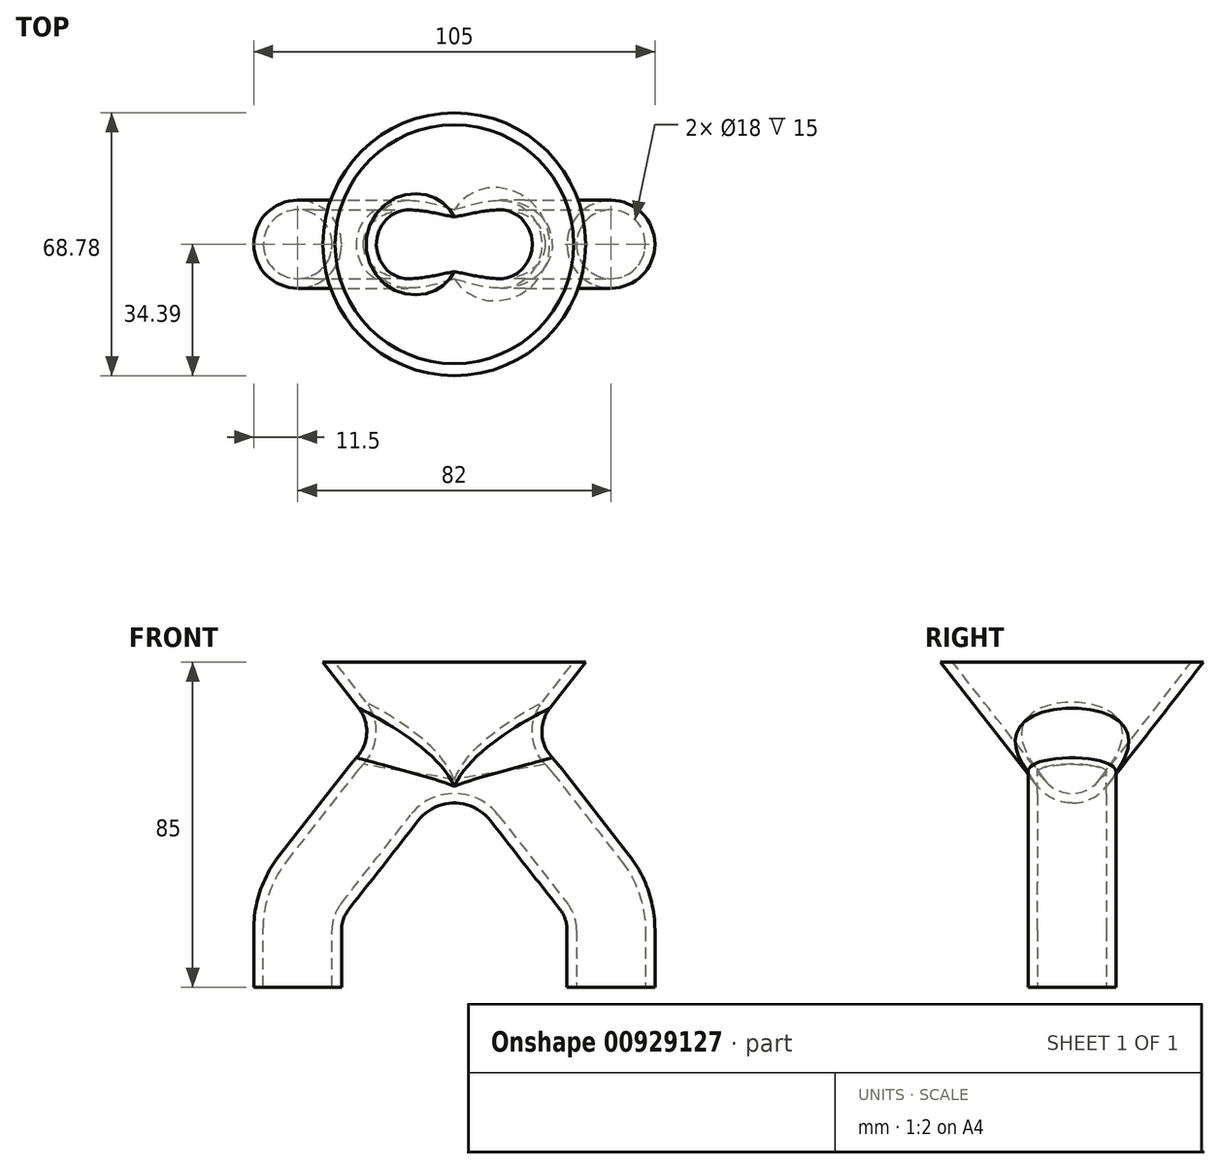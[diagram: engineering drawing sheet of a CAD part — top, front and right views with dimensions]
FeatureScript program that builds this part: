
annotation { "Feature Type Name" : "Feature", "Feature Type Description" : "" }
export const myFeature = defineFeature(function(context is Context, id is Id, definition is map)
    precondition{}
    {
        {
            var Q0;
            Q0=qCreatedBy(makeId("Front.planeOp"),FACE);
            var sketch = newSketch(context, id + "F0", { "sketchPlane" : qUnion([Q0])});
            skLineSegment(sketch, "E0", {"start": v(-41, 0) * mm, "end": v(-41, 15) * mm});
            skLineSegment(sketch, "E1", {"start": v(41, 0) * mm, "end": v(41, 15) * mm});
            skLineSegment(sketch, "E2", {"start": v(-36.76, 27.31) * mm, "end": v(-18.56, 50.6) * mm});
            skLineSegment(sketch, "E3", {"start": v(18.56, 50.6) * mm, "end": v(36.76, 27.31) * mm});
            skPoint(sketch, "E4.visualSharp", {"position": v(-41, 21.89) * mm});
            skArc(sketch, "E4.filletArc", {"start": v(-36.76, 27.31) * mm, "mid": v(-39.91, 21.51) * mm, "end": v(-41, 15) * mm});
            skPoint(sketch, "E5.visualSharp", {"position": v(41, 21.89) * mm});
            skArc(sketch, "E5.filletArc", {"start": v(41, 15) * mm, "mid": v(39.91, 21.51) * mm, "end": v(36.76, 27.31) * mm});
            skArc(sketch, "E6.filletArc", {"start": v(18.56, 50.6) * mm, "mid": v(0, 59.66) * mm, "end": v(-18.56, 50.6) * mm});
            skSolve(sketch);
        }
        {
            var Q0;
            Q0=qCreatedBy(makeId("Top.planeOp"),FACE);
            var sketch = newSketch(context, id + "F1", { "sketchPlane" : qUnion([Q0])});
            skPoint(sketch, "E7.0", {"position": v(-41, 0) * mm});
            skCircle(sketch, "E8", {"center": v(-41, 0) * mm, "radius": 11.5 * mm});
            skSolve(sketch);
        }
        {
            var Q0;
            Q0=makeQuery(id+"F1.imprint","IMPRINT",FACE,{"disambiguationData":[TD([[makeQuery(id+"F1.imprint","IMPRINT",EDGE,{"derivedFrom":sQuery(id+"F1.wireOp",EDGE,"E8")}),1.0]])]});
            var Q1;
            Q1=sQuery(id+"F0.wireOp",EDGE,"E0");
            var Q2;
            Q2=sQuery(id+"F0.wireOp",EDGE,"E4.filletArc");
            var Q3;
            Q3=sQuery(id+"F0.wireOp",EDGE,"E2");
            var Q4;
            Q4=sQuery(id+"F0.wireOp",EDGE,"E6.filletArc");
            var Q5;
            Q5=sQuery(id+"F0.wireOp",EDGE,"E3");
            var Q6;
            Q6=sQuery(id+"F0.wireOp",EDGE,"E5.filletArc");
            var Q7;
            Q7=sQuery(id+"F0.wireOp",EDGE,"E1");
            sweep(context, id + "F2", {"profiles" : qUnion([Q0]), "path" : qUnion([Q1, Q2, Q3, Q4, Q5, Q6, Q7])});
        }
        {
            var Q0;
            Q0=qCreatedBy(makeId("Right.planeOp"),FACE);
            var sketch = newSketch(context, id + "F3", { "sketchPlane" : qUnion([Q0])});
            skCircle(sketch, "E9", {"center": v(0, 59.66) * mm, "radius": 11.5 * mm});
            skLineSegment(sketch, "E10", {"start": v(0, 59.66) * mm, "end": v(0, 85) * mm});
            skLineSegment(sketch, "E11", {"start": v(0, 85) * mm, "end": v(34.4, 85) * mm});
            skLineSegment(sketch, "E12", {"start": v(34.4, 85) * mm, "end": v(9.06, 52.58) * mm});
            skSolve(sketch);
        }
        {
            var Q0;
            {var subQ4=sQuery(id+"F3.wireOp",EDGE,"E11");Q0=makeQuery(id+"F3.imprint","IMPRINT",FACE,{"disambiguationData":[TD([[makeQuery(id+"F3.imprint","IMPRINT",EDGE,{"derivedFrom":subQ4}),-1.0]])]});}
            var Q1;
            Q1=sQuery(id+"F3.wireOp",EDGE,"E10");
            revolve(context, id + "F4", {"operationType" : NewBodyOperationType.ADD, "surfaceOperationType" : NewSurfaceOperationType.NEW, "entities" : qUnion([Q0]), "axis" : qUnion([Q1]), "revolveType" : RevolveType.FULL});
        }
        {
            var Q0;
            Q0=makeQuery(id+"F4.boolean.opBoolean","INTERSECT",EDGE,{"disambiguationData":[OD(0.0)],"derivedFrom":[makeQuery(id+"F2.opSweep","SWEPT_FACE",FACE,{"disambiguationData":[OSD([sQuery(id+"F0.wireOp",EDGE,"E6.filletArc"),sQuery(id+"F1.wireOp",EDGE,"E8")])]}),makeQuery(id+"F4.opRevolve","SWEPT_FACE",FACE,{"disambiguationData":[OSD([sQuery(id+"F3.wireOp",EDGE,"E12")])]})]});
            var Q1;
            Q1=makeQuery(id+"F4.boolean.opBoolean","INTERSECT",EDGE,{"disambiguationData":[OD(1.0)],"derivedFrom":[makeQuery(id+"F2.opSweep","SWEPT_FACE",FACE,{"disambiguationData":[OSD([sQuery(id+"F0.wireOp",EDGE,"E6.filletArc"),sQuery(id+"F1.wireOp",EDGE,"E8")])]}),makeQuery(id+"F4.opRevolve","SWEPT_FACE",FACE,{"disambiguationData":[OSD([sQuery(id+"F3.wireOp",EDGE,"E12")])]})]});
            fillet(context, id + "F5", {"entities" : qUnion([Q0, Q1]), "radius" : 10 * mm, "tangentPropagation" : true, "allowEdgeOverflow" : false});
        }
        {
            var Q0;
            Q0=makeQuery(id+"F4.opRevolve","SWEPT_FACE",FACE,{"disambiguationData":[OSD([sQuery(id+"F3.wireOp",EDGE,"E11")])]});
            var Q1;
            Q1=makeQuery(id+"F2.opSweep","CAP_FACE",FACE,{"disambiguationData":[OSD([sQuery(id+"F0.wireOp",VERTEX,"E0.start"),sQuery(id+"F1.wireOp",EDGE,"E8")])],"isStart":true});
            var Q2;
            Q2=makeQuery(id+"F2.opSweep","CAP_FACE",FACE,{"disambiguationData":[OSD([sQuery(id+"F0.wireOp",VERTEX,"E1.start"),sQuery(id+"F1.wireOp",EDGE,"E8")])],"isStart":false});
            shell(context, id + "F6", {"entities" : qUnion([Q0, Q1, Q2]), "thickness" : 2.5 * mm});
        }
    });
